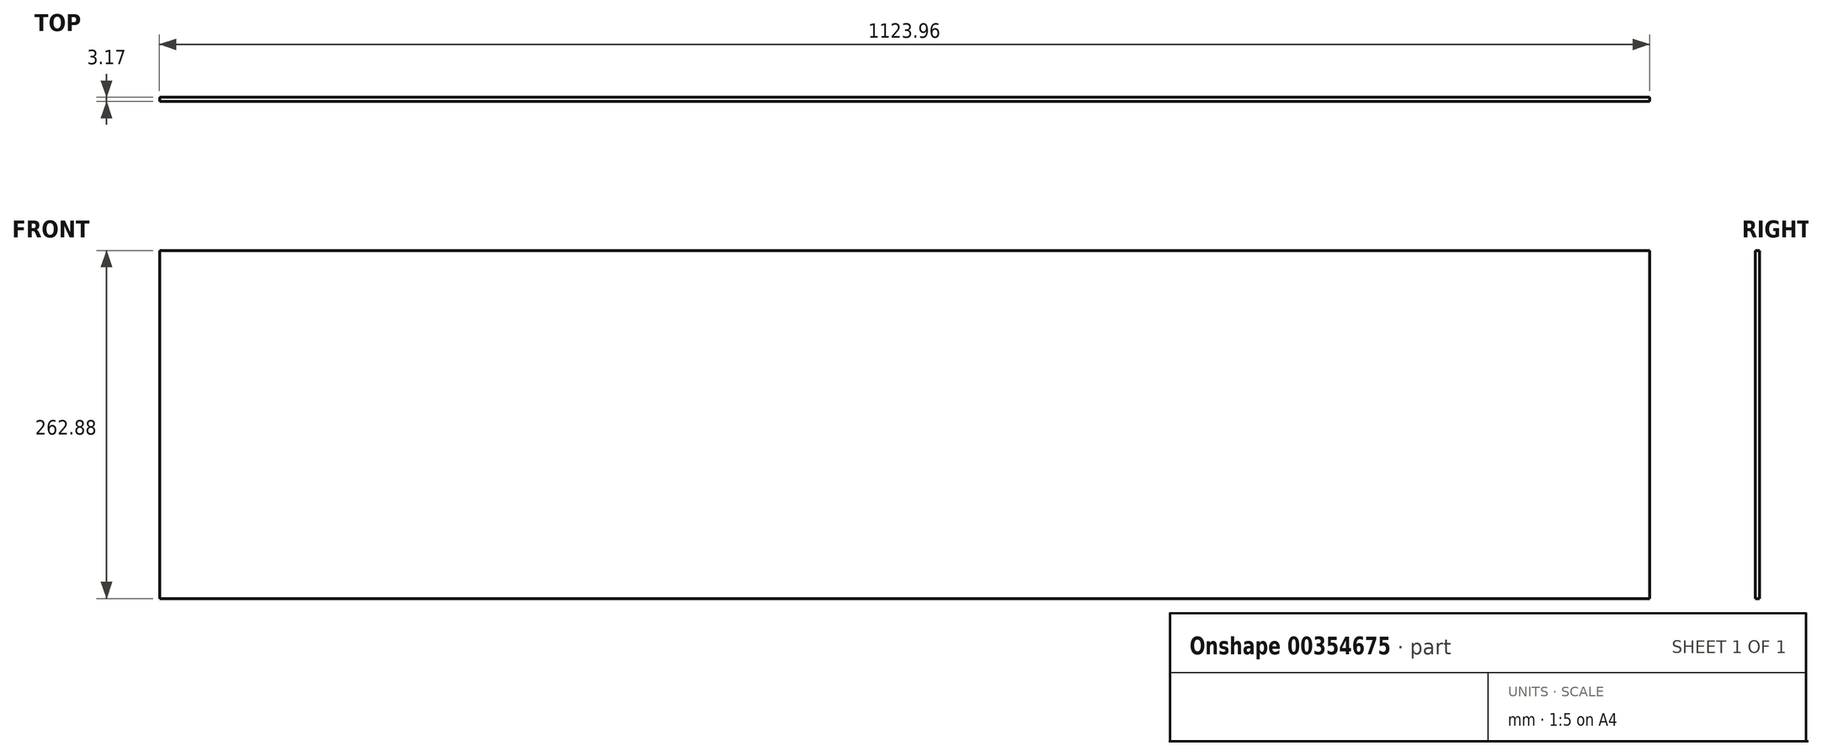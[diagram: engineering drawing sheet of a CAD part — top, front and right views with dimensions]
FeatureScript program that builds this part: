
annotation { "Feature Type Name" : "Feature", "Feature Type Description" : "" }
export const myFeature = defineFeature(function(context is Context, id is Id, definition is map)
    precondition{}
    {
        {
            var Q0;
            Q0=qCreatedBy(makeId("Front.planeOp"),FACE);
            var sketch = newSketch(context, id + "F0", { "sketchPlane" : qUnion([Q0])});
            skLineSegment(sketch, "E0.bottom", {"start": v(561.98, 131.44) * mm, "end": v(-561.98, 131.45) * mm});
            skLineSegment(sketch, "E0.top", {"start": v(561.98, -131.44) * mm, "end": v(-561.98, -131.44) * mm});
            skLineSegment(sketch, "E0.left", {"start": v(561.98, 131.44) * mm, "end": v(561.98, -131.45) * mm});
            skLineSegment(sketch, "E0.right", {"start": v(-561.97, 131.45) * mm, "end": v(-561.98, -131.45) * mm});
            skPoint(sketch, "E0.middle", {"position": v(0, 0) * mm});
            skSolve(sketch);
        }
        {
            var Q0;
            Q0=qSketchRegion(id+"F0",true);
            extrude(context, id + "F1", {"entities" : qUnion([Q0]), "depth" : 3.17 * mm});
        }
    });
